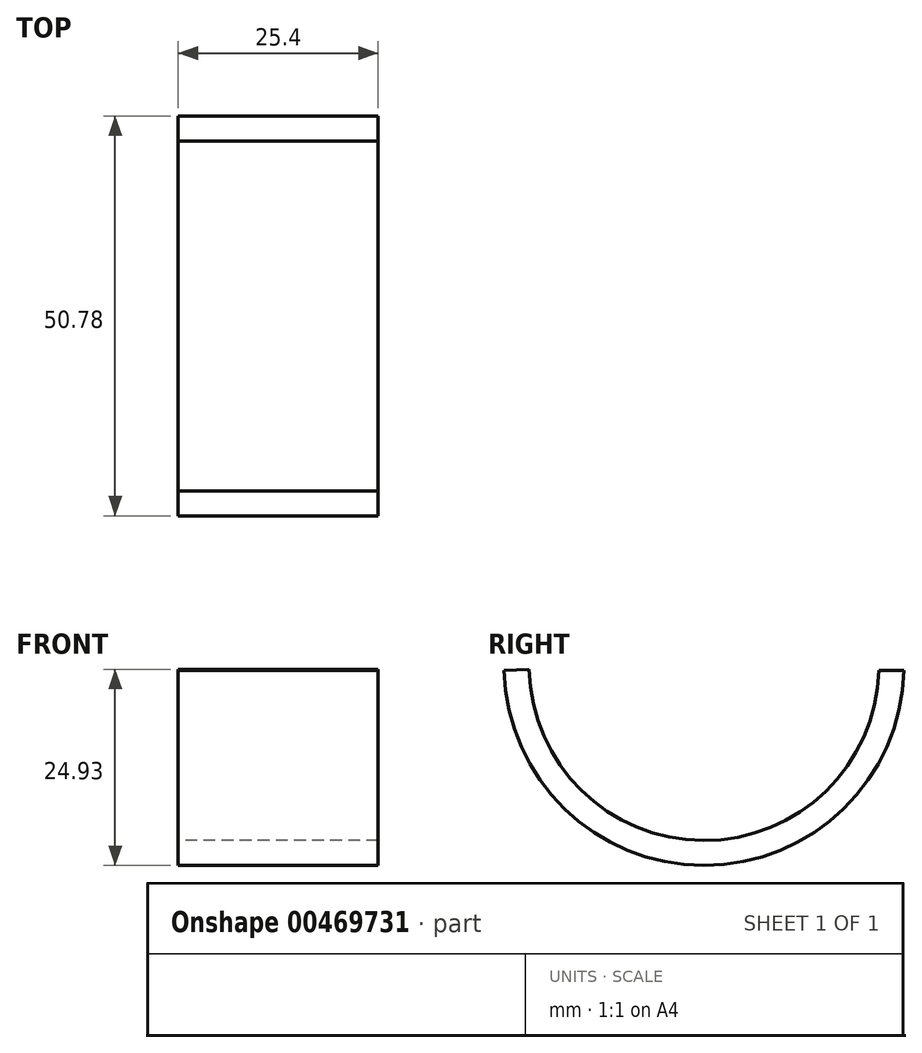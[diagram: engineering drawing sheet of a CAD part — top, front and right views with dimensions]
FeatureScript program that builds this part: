
annotation { "Feature Type Name" : "Feature", "Feature Type Description" : "" }
export const myFeature = defineFeature(function(context is Context, id is Id, definition is map)
    precondition{}
    {
        {
            var Q0;
            Q0=qCreatedBy(makeId("Right.planeOp"),FACE);
            var sketch = newSketch(context, id + "F0", { "sketchPlane" : qUnion([Q0])});
            skArc(sketch, "E0", {"start": v(-50.78, 0) * mm, "mid": v(-25.4, -24.77) * mm, "end": v(0, 0) * mm});
            skSolve(sketch);
        }
        {
            var Q0;
            Q0=qCreatedBy(makeId("Top.planeOp"),FACE);
            var sketch = newSketch(context, id + "F1", { "sketchPlane" : qUnion([Q0])});
            skLineSegment(sketch, "E1.bottom", {"start": v(0, 0) * mm, "end": v(25.4, 0) * mm});
            skLineSegment(sketch, "E1.top", {"start": v(0, -3.18) * mm, "end": v(25.4, -3.18) * mm});
            skLineSegment(sketch, "E1.left", {"start": v(0, 0) * mm, "end": v(0, -3.18) * mm});
            skLineSegment(sketch, "E1.right", {"start": v(25.4, 0) * mm, "end": v(25.4, -3.18) * mm});
            skSolve(sketch);
        }
        {
            var Q0;
            Q0=makeQuery(id+"F1.imprint","IMPRINT",FACE,{"disambiguationData":[TD([[makeQuery(id+"F1.imprint","IMPRINT",EDGE,{"derivedFrom":sQuery(id+"F1.wireOp",EDGE,"E1.bottom")}),-1.0]])]});
            var Q1;
            Q1=sQuery(id+"F0.wireOp",EDGE,"E0");
            sweep(context, id + "F2", {"profiles" : qUnion([Q0]), "path" : qUnion([Q1])});
        }
    });
